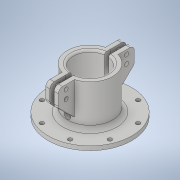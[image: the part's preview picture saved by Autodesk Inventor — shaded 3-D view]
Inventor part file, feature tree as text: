
AUTODESK INVENTOR PART (.ipt)
format: ipt  version: 2020 (Build 240168000, 168)  size: 636,928 bytes
history: native  units: in
note: dims shown in document units (in); Inventor stores cm internally (conversion verified against a paired STEP export)
features: extrude x8, fillet x7, sketch x7, chamfer x1, pattern_circular x1
ambient origin geometry x8: Origin, YZ Plane, XZ Plane, XY Plane, X Axis, Y Axis, Z Axis, Center Point
bodies: Solid1 (feature_tree)
feature tree (24):
  extrude  "Extrusion1"  Depth=1.0in
  extrude  "Extrusion3"  Depth=0.125in
  extrude  "Extrusion4"  Depth=0.5in
  extrude  "Extrusion5"  Depth=0.125in
  chamfer  "Chamfer1"  Distance=0.5in
  fillet  "Fillet1"  Radius=1.0in
  extrude  "Extrusion6"  Depth=2.5in
  extrude  "Extrusion7"  Depth=0.125in TaperAngle=0.0deg
  fillet  "Fillet2"  Radius=0.125in
  extrude  "Extrusion8"  Depth=1.0in
  fillet  "Fillet3"  Radius=3.1496in
  fillet  "Fillet4"  Radius=0.0625in
  fillet  "Fillet5"  Radius=0.125in
  fillet  "Fillet6"  Radius=0.2in
  extrude  "Extrusion9"  Depth=2.0in TaperAngle=0.0deg
  pattern_circular  "Circular Pattern1"  [2 undecoded]
  fillet  "Fillet7"  Radius=0.0625in
  sketch  "Sketch1"  dims[d0=1.35in d1=1.0in]
  sketch  "Sketch3"  dims[d2=1.25in d3=0.0in d7=0.125in]
  sketch  "Sketch4"  dims[d8=1.0in d9=0.0in d13=0.5in]
  sketch  "Sketch6"  dims[d18=0.5in d19=0.0in d21=0.125in]
  sketch  "Sketch7"  dims[d22=0.125in]
  sketch  "Sketch8"  dims[d23=0.125in d26=0.5in d27=0.0in]
  sketch  "Sketch9"  dims[d28=0.468in d29=0.448in d30=45.0deg d32=1.0in d33=2.5in d34=0.125in d35=0.0in d36=0.125in d37=1.0in d38=3.1496in d40=360.0deg d42=0.0625in d43=0.0in d44=0.125in d45=0.2in d46=2.0in d47=0.0in d48=0.125in d49=0.0625in d50=0.0625in d51=0.025in d52=1.1in d53=22.5deg d54=0.125in d55=2.0in d56=0.0in d57=3.1496in d58=360.0deg d64=0.125in d65=0.125in d66=0.064in d68=0.2295in d69=0.2295in d70=0.125in d71=0.125in]
note: 2 required parameter values undecoded (feature->parameter linkage not recoverable at this tier; creation-order binding heuristic only, values carry confidence <= 0.55)
